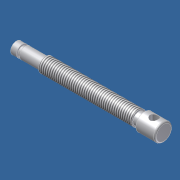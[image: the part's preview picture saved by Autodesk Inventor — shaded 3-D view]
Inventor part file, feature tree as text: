
AUTODESK INVENTOR PART (.ipt)
format: ipt  version: unknown  size: 208,896 bytes
history: native  units: in
note: dims shown in document units (in); Inventor stores cm internally (conversion verified against a paired STEP export)
features: sketch x2, revolve x1, thread x1, plane x1, hole x1, fillet x1
ambient origin geometry x8: Origin, YZ Plane, XZ Plane, XY Plane, X Axis, Y Axis, Z Axis, Center Point
bodies: Solid1 (feature_tree)
feature tree (7):
  revolve  "Revolution1"  [1 undecoded]
  thread  "Thread1"  [1 undecoded]
  plane  "Work Plane1"
  hole  "Hole1"  [1 undecoded]
  fillet  "Fillet1"  Radius=0.812in
  sketch  "Sketch1"  dims[d0=0.375in d1=6.25in d2=0.25in]
  sketch  "Sketch2"  dims[d5=0.25in d6=0.25in d7=0.812in d10=0.25in d12=0.3125in d13=0.25in d14=3.937in d16=0.1875in d18=90.0deg d19=1.0in d20=0.0in d21=0.406in d22=0.3438in d23=0.75in d24=0.375in d25=0.25in d26=0.5635in d27=1.0in d28=0.0in d29=0.062in d33=0.1295in]
note: 3 required parameter values undecoded (feature->parameter linkage not recoverable at this tier; creation-order binding heuristic only, values carry confidence <= 0.55)